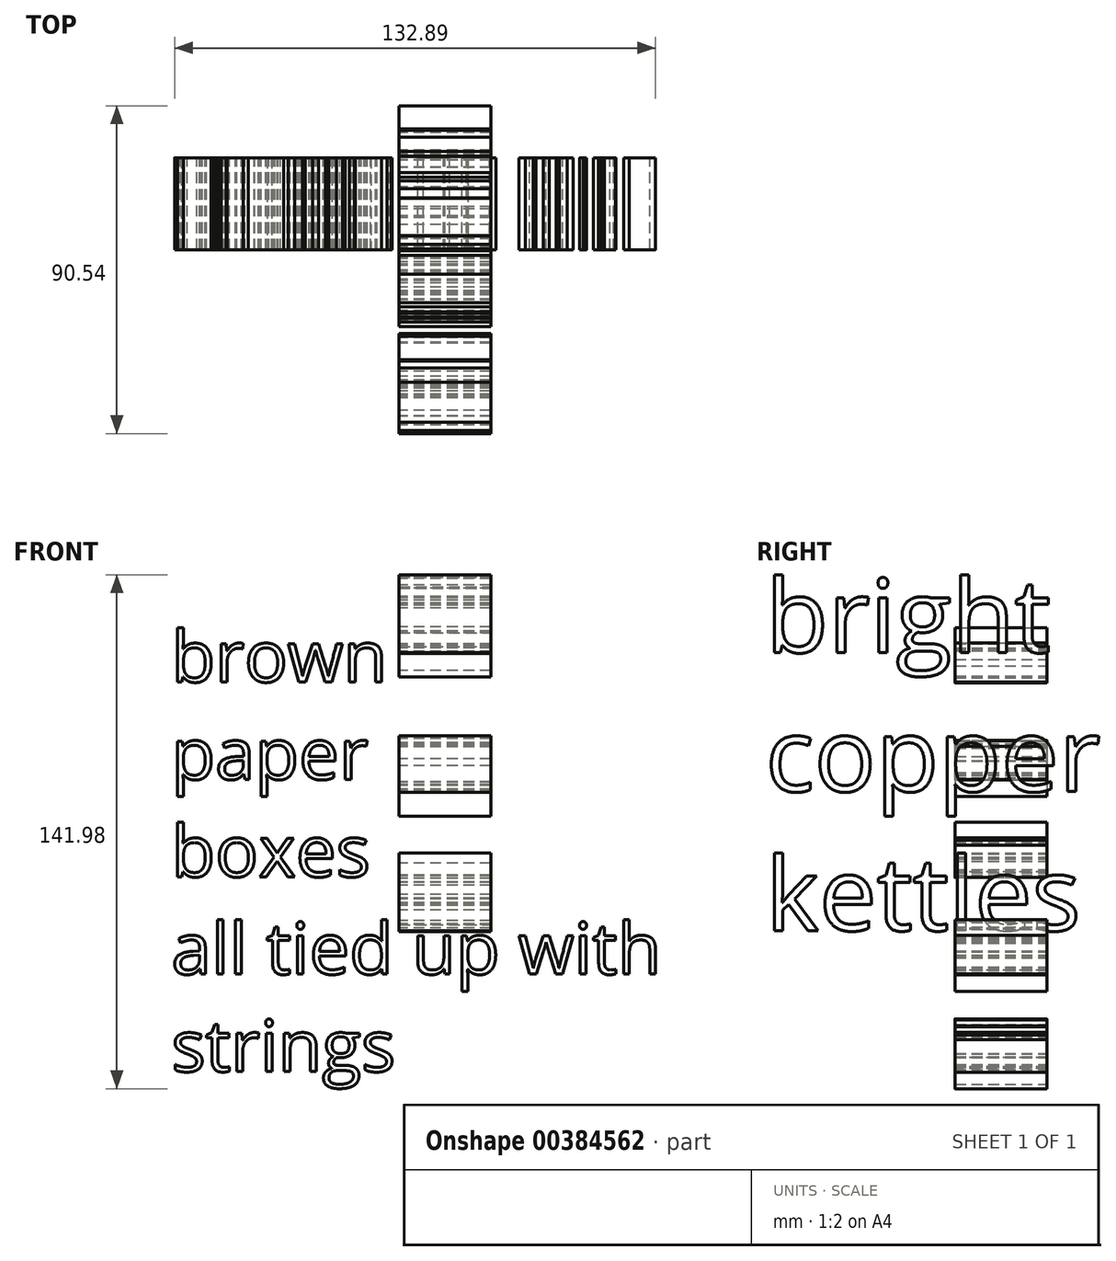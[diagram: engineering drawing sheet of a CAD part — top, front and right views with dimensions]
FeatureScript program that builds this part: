
annotation { "Feature Type Name" : "Feature", "Feature Type Description" : "" }
export const myFeature = defineFeature(function(context is Context, id is Id, definition is map)
    precondition{}
    {
        {
            var Q0;
            Q0=qCreatedBy(makeId("Right.planeOp"),FACE);
            var sketch = newSketch(context, id + "F0", { "sketchPlane" : qUnion([Q0])});
            skText(sketch, "E0", { "text": "bright\ncopper\nkettles", "fontName": "OpenSans-Regular.ttf"});
            const initialGuessF0  = {"E0": [-0.07775, 0.04385, 1, 0, 0.02034]};
            skSetInitialGuess(sketch, initialGuessF0);
            skSolve(sketch);
        }
        {
            var Q0;
            Q0 = qSketchRegion(id + "F0", true);
            extrude(context, id + "F1", {"entities" : qUnion([Q0]), "depth" : 25.4 * mm});
        }
        {
            var Q0;
            Q0=qCreatedBy(makeId("Front.planeOp"),FACE);
            var sketch = newSketch(context, id + "F2", { "sketchPlane" : qUnion([Q0])});
            skText(sketch, "E1", { "text": "brown\npaper\nboxes\nall tied up with\nstrings", "fontName": "OpenSans-Regular.ttf"});
            const initialGuessF2  = {"E1": [-0.06292, 0.03568, 1, 0, 0.01424]};
            skSetInitialGuess(sketch, initialGuessF2);
            skSolve(sketch);
        }
        {
            var Q0;
            Q0 = qSketchRegion(id + "F2", true);
            extrude(context, id + "F3", {"entities" : qUnion([Q0]), "depth" : 25.4 * mm});
        }
    });
